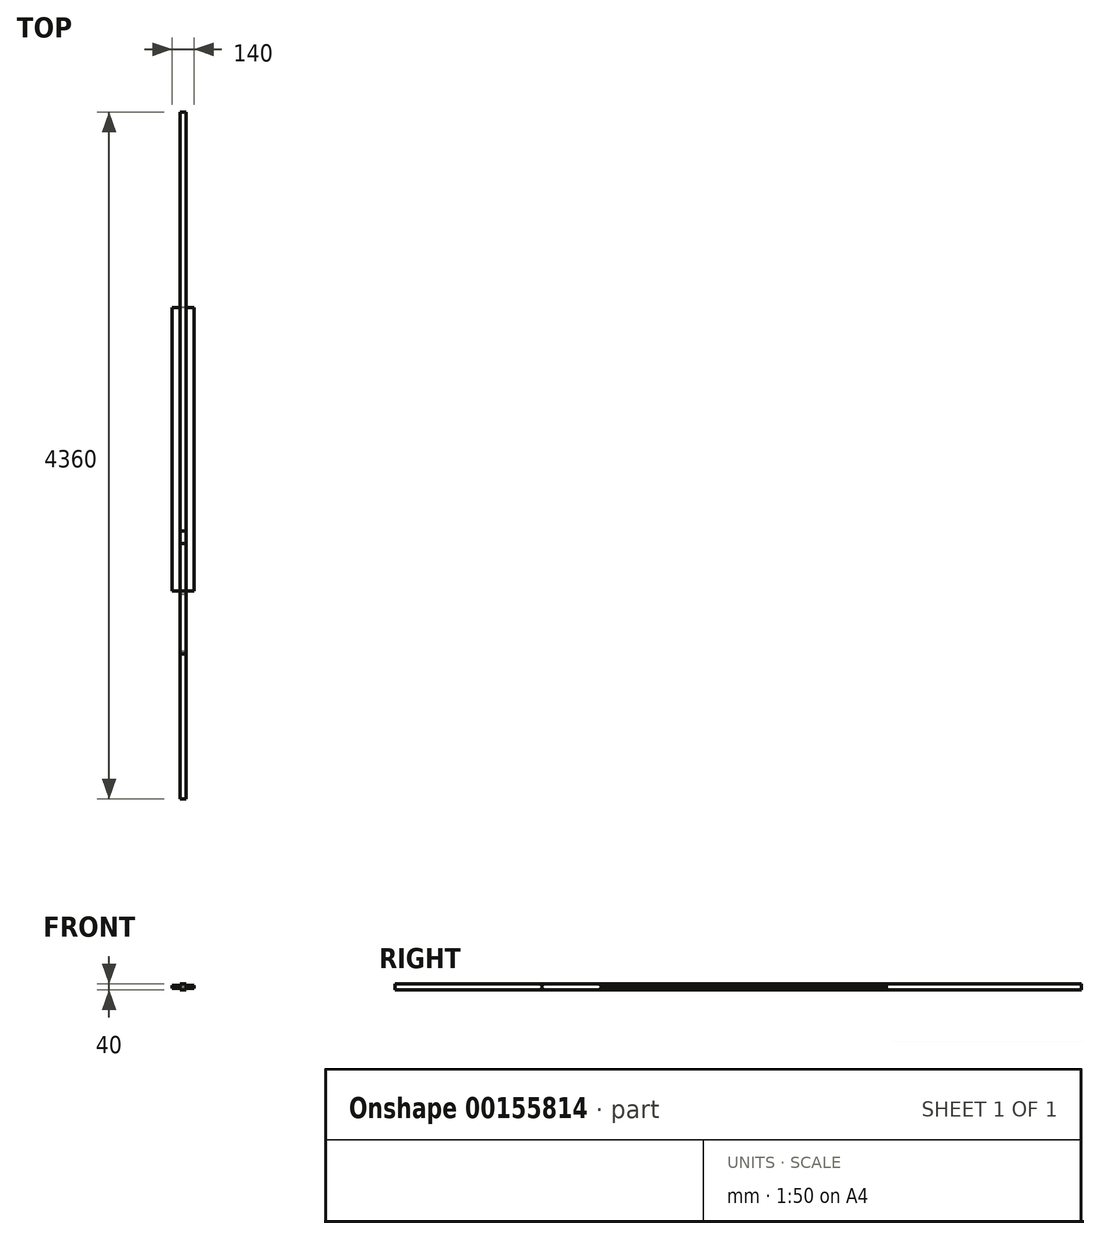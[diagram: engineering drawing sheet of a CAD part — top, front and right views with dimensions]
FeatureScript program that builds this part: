
annotation { "Feature Type Name" : "Feature", "Feature Type Description" : "" }
export const myFeature = defineFeature(function(context is Context, id is Id, definition is map)
    precondition{}
    {
        {
            var Q0;
            Q0=qCreatedBy(makeId("Front.planeOp"),FACE);
            var sketch = newSketch(context, id + "F0", { "sketchPlane" : qUnion([Q0])});
            skLineSegment(sketch, "E0.bottom", {"start": v(70, -10) * mm, "end": v(-70, -10) * mm});
            skLineSegment(sketch, "E0.top", {"start": v(70, 10) * mm, "end": v(-70, 10) * mm});
            skLineSegment(sketch, "E0.left", {"start": v(70, -10) * mm, "end": v(70, 10) * mm});
            skLineSegment(sketch, "E0.right", {"start": v(-70, -10) * mm, "end": v(-70, 10) * mm});
            skPoint(sketch, "E0.middle", {"position": v(0, 0) * mm});
            skSolve(sketch);
        }
        {
            var Q0;
            Q0 = qSketchRegion(id + "F0", true);
            extrude(context, id + "F1", {"entities" : qUnion([Q0]), "oppositeDirection" : true, "depth" : 1800 * mm});
        }
        {
            var Q0;
            Q0=qCreatedBy(makeId("Front.planeOp"),FACE);
            var sketch = newSketch(context, id + "F2", { "sketchPlane" : qUnion([Q0])});
            skLineSegment(sketch, "E1.bottom", {"start": v(20, -20) * mm, "end": v(-20, -20) * mm});
            skLineSegment(sketch, "E1.top", {"start": v(20, 20) * mm, "end": v(-20, 20) * mm});
            skLineSegment(sketch, "E1.left", {"start": v(20, -20) * mm, "end": v(20, 20) * mm});
            skLineSegment(sketch, "E1.right", {"start": v(-20, -20) * mm, "end": v(-20, 20) * mm});
            skPoint(sketch, "E1.middle", {"position": v(0, 0) * mm});
            skSolve(sketch);
        }
        {
            var Q0;
            Q0 = qSketchRegion(id + "F2", true);
            extrude(context, id + "F3", {"entities" : qUnion([Q0]), "oppositeDirection" : true, "depth" : 380 * mm});
        }
        {
            var Q0;
            Q0 = qSketchRegion(id + "F2", true);
            extrude(context, id + "F4", {"entities" : qUnion([Q0]), "depth" : 400 * mm});
        }
        {
            var Q0;
            Q0=makeQuery(id+"F4.opExtrude","SWEPT_FACE",FACE,{"disambiguationData":[OSD([sQuery(id+"F2.wireOp",EDGE,"E1.left")])]});
            var sketch = newSketch(context, id + "F5", { "sketchPlane" : qUnion([Q0])});
            skLineSegment(sketch, "E2", {"start": v(-400, 0) * mm, "end": v(0, 0) * mm, "construction": true});
            skLineSegment(sketch, "E3", {"start": v(0, 20) * mm, "end": v(0, -20) * mm});
            skLineSegment(sketch, "E4", {"start": v(0, -20) * mm, "end": v(-20, 0) * mm});
            skLineSegment(sketch, "E5", {"start": v(-20, 0) * mm, "end": v(0, 20) * mm});
            skLineSegment(sketch, "E6", {"start": v(-400, 20) * mm, "end": v(-400, -20) * mm});
            skLineSegment(sketch, "E7", {"start": v(-400, -20) * mm, "end": v(-380, 0) * mm});
            skLineSegment(sketch, "E8", {"start": v(-380, 0) * mm, "end": v(-400, 20) * mm});
            skSolve(sketch);
        }
        {
            var Q0;
            Q0 = qSketchRegion(id + "F5", true);
            extrude(context, id + "F6", {"entities" : qUnion([Q0]), "operationType" : NewBodyOperationType.REMOVE, "oppositeDirection" : true, "depth" : 84 * mm});
        }
        {
            var Q0;
            Q0 = qSketchRegion(id + "F2", true);
            extrude(context, id + "F7", {"entities" : qUnion([Q0]), "oppositeDirection" : true, "depth" : 300 * mm});
        }
        {
            var Q0;
            Q0 = qSketchRegion(id + "F2", true);
            extrude(context, id + "F8", {"entities" : qUnion([Q0]), "depth" : 1320 * mm});
        }
        {
            var Q0;
            Q0 = qSketchRegion(id + "F2", true);
            extrude(context, id + "F9", {"entities" : qUnion([Q0]), "oppositeDirection" : true, "depth" : 3040 * mm});
        }
    });
